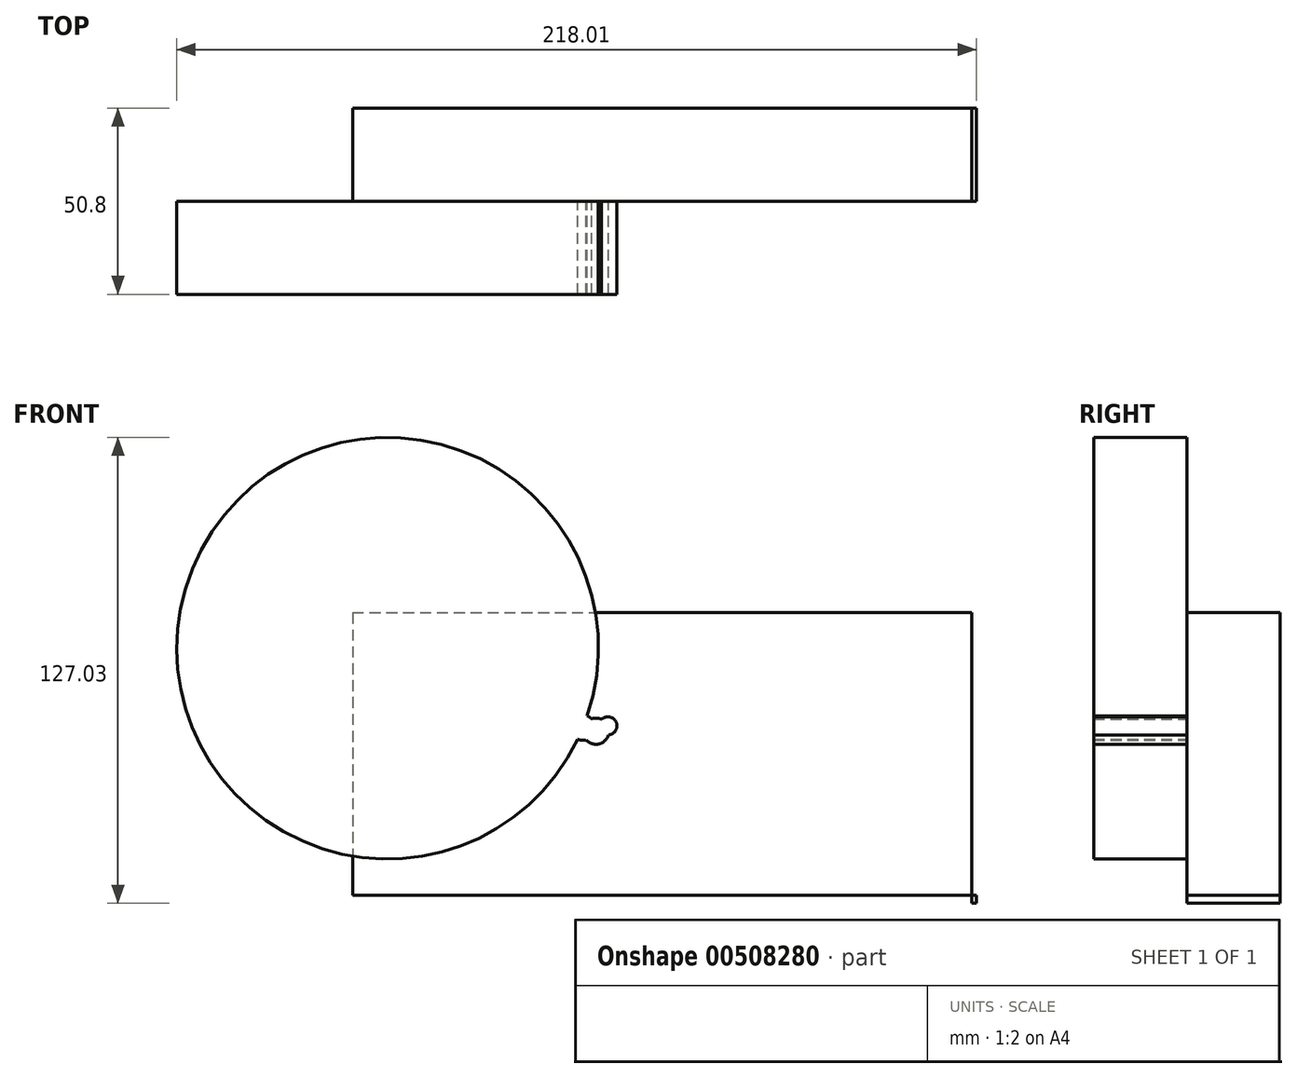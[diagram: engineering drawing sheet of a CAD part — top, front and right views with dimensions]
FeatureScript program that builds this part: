
annotation { "Feature Type Name" : "Feature", "Feature Type Description" : "" }
export const myFeature = defineFeature(function(context is Context, id is Id, definition is map)
    precondition{}
    {
        {
            var Q0;
            Q0=qCreatedBy(makeId("Front.planeOp"),FACE);
            var sketch = newSketch(context, id + "F0", { "sketchPlane" : qUnion([Q0])});
            skLineSegment(sketch, "E0.bottom", {"start": v(-87.83, 43.65) * mm, "end": v(81.05, 43.65) * mm});
            skLineSegment(sketch, "E0.top", {"start": v(-87.83, -33.36) * mm, "end": v(81.05, -33.36) * mm});
            skLineSegment(sketch, "E0.left", {"start": v(-87.83, 43.65) * mm, "end": v(-87.83, -33.36) * mm});
            skLineSegment(sketch, "E0.right", {"start": v(81.05, 43.65) * mm, "end": v(81.05, -33.36) * mm});
            skLineSegment(sketch, "E1.bottom", {"start": v(81.05, -33.36) * mm, "end": v(82.23, -33.36) * mm});
            skLineSegment(sketch, "E1.top", {"start": v(81.05, -35.57) * mm, "end": v(82.23, -35.57) * mm});
            skLineSegment(sketch, "E1.left", {"start": v(81.05, -33.36) * mm, "end": v(81.05, -35.57) * mm});
            skLineSegment(sketch, "E1.right", {"start": v(82.23, -33.36) * mm, "end": v(82.23, -35.57) * mm});
            skSolve(sketch);
        }
        {
            var Q0;
            Q0 = qSketchRegion(id + "F0", true);
            extrude(context, id + "F1", {"entities" : qUnion([Q0]), "depth" : 25.4 * mm});
        }
        {
            var Q0;
            Q0=makeQuery(id+"F1.opExtrude","CAP_FACE",FACE,{"disambiguationData":[OSD([sQuery(id+"F0.wireOp",EDGE,"E0.bottom"),sQuery(id+"F0.wireOp",EDGE,"E0.top"),sQuery(id+"F0.wireOp",EDGE,"E0.left"),sQuery(id+"F0.wireOp",EDGE,"E0.right")])],"isStart":false});
            var sketch = newSketch(context, id + "F2", { "sketchPlane" : qUnion([Q0])});
            skCircle(sketch, "E2", {"center": v(-78.3, 33.98) * mm, "radius": 57.49 * mm});
            skCircle(sketch, "E3", {"center": v(-25.06, 12.28) * mm, "radius": 3.42 * mm});
            skCircle(sketch, "E4", {"center": v(-21.5, 11.35) * mm, "radius": 3.57 * mm});
            skCircle(sketch, "E5", {"center": v(-18.24, 12.8) * mm, "radius": 2.48 * mm});
            skSolve(sketch);
        }
        {
            var Q0;
            Q0 = qSketchRegion(id + "F2", true);
            extrude(context, id + "F3", {"entities" : qUnion([Q0]), "operationType" : NewBodyOperationType.ADD, "depth" : 25.4 * mm});
        }
    });
